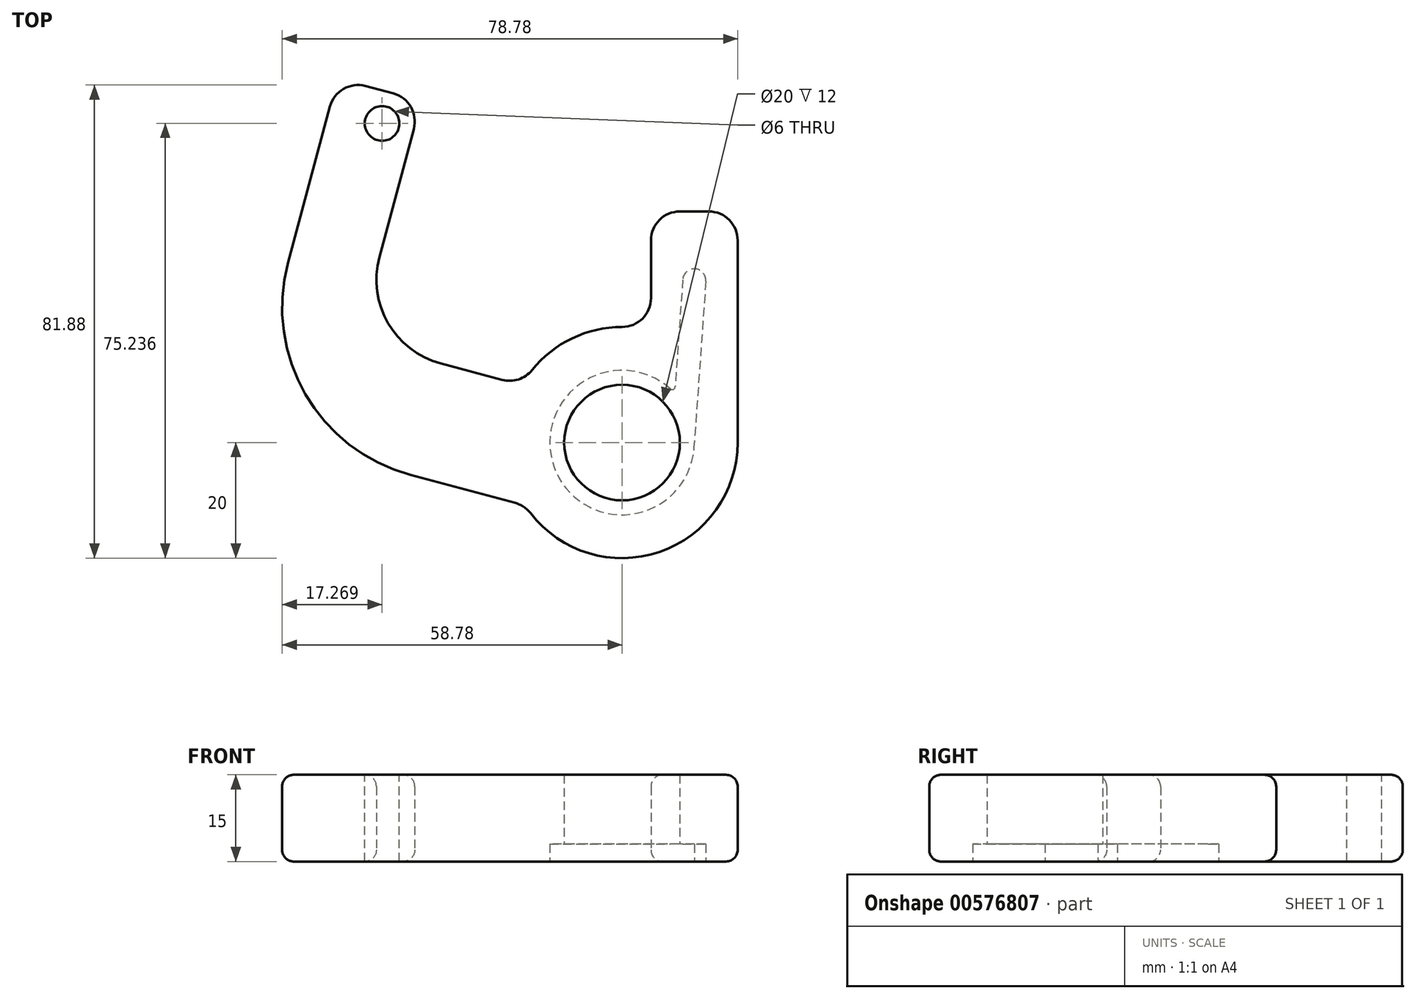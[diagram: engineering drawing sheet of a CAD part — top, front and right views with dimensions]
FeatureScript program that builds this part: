
annotation { "Feature Type Name" : "Feature", "Feature Type Description" : "" }
export const myFeature = defineFeature(function(context is Context, id is Id, definition is map)
    precondition{}
    {
        {
            var Q0;
            Q0=qCreatedBy(makeId("Top.planeOp"),FACE);
            var sketch = newSketch(context, id + "F0", { "sketchPlane" : qUnion([Q0])});
            skCircle(sketch, "E0", {"center": v(0, 0) * mm, "radius": 10 * mm});
            skCircle(sketch, "E1", {"center": v(0, 0) * mm, "radius": 20 * mm});
            skLineSegment(sketch, "E2", {"start": v(20, 0) * mm, "end": v(20, 40) * mm});
            skLineSegment(sketch, "E3", {"start": v(20, 40) * mm, "end": v(5, 40) * mm});
            skLineSegment(sketch, "E4", {"start": v(5, 40) * mm, "end": v(5, 19.36) * mm});
            skLineSegment(sketch, "E5", {"start": v(-17.35, 9.95) * mm, "end": v(-31.37, 13.7) * mm});
            skLineSegment(sketch, "E6", {"start": v(-57.76, 31.13) * mm, "end": v(-49.22, 63) * mm});
            skLineSegment(sketch, "E7", {"start": v(-49.22, 63) * mm, "end": v(-34.73, 59.12) * mm});
            skLineSegment(sketch, "E8", {"start": v(-34.73, 59.12) * mm, "end": v(-41.98, 32.08) * mm});
            skLineSegment(sketch, "E9", {"start": v(0, 0) * mm, "end": v(-115.9, 0) * mm, "construction": true});
            skLineSegment(sketch, "E10", {"start": v(-16.76, -10.92) * mm, "end": v(-36.55, -5.61) * mm});
            skPoint(sketch, "E11.visualSharp", {"position": v(-65.53, 2.15) * mm});
            skArc(sketch, "E11.filletArc", {"start": v(-57.76, 31.13) * mm, "mid": v(-54.77, 8.36) * mm, "end": v(-36.55, -5.61) * mm});
            skPoint(sketch, "E12.visualSharp", {"position": v(-45.86, 17.59) * mm});
            skArc(sketch, "E12.filletArc", {"start": v(-41.98, 32.08) * mm, "mid": v(-40.48, 20.7) * mm, "end": v(-31.37, 13.7) * mm});
            skSolve(sketch);
        }
        {
            var Q0;
            {var subQ0=sQuery(id+"F0.wireOp",EDGE,"E5");Q0=makeQuery(id+"F0.imprint","IMPRINT",FACE,{"disambiguationData":[TD([[makeQuery(id+"F0.imprint","IMPRINT",EDGE,{"derivedFrom":subQ0}),1.0]])]});}
            var Q1;
            Q1=makeQuery(id+"F0.imprint","IMPRINT",FACE,{"disambiguationData":[TD([[makeQuery(id+"F0.imprint","IMPRINT",EDGE,{"derivedFrom":sQuery(id+"F0.wireOp",EDGE,"E0")}),-1.0]])]});
            var Q2;
            {var subQ0=sQuery(id+"F0.wireOp",EDGE,"E2");Q2=makeQuery(id+"F0.imprint","IMPRINT",FACE,{"disambiguationData":[TD([[makeQuery(id+"F0.imprint","IMPRINT",EDGE,{"derivedFrom":subQ0}),1.0]])]});}
            extrude(context, id + "F1", {"entities" : qUnion([Q0, Q1, Q2]), "depth" : 15 * mm, "offsetDistance" : 25 * mm});
        }
        {
            var Q0;
            Q0=makeQuery(id+"F1.opExtrude","SWEPT_EDGE",EDGE,{"disambiguationData":[OSD([sQuery(id+"F0.wireOp",EDGE,"E1"),sQuery(id+"F0.wireOp",EDGE,"E5")])]});
            var Q1;
            Q1=makeQuery(id+"F1.opExtrude","SWEPT_EDGE",EDGE,{"disambiguationData":[OSD([sQuery(id+"F0.wireOp",EDGE,"E1"),sQuery(id+"F0.wireOp",EDGE,"E4")])]});
            fillet(context, id + "F2", {"entities" : qUnion([Q0, Q1]), "radius" : 5 * mm, "tangentPropagation" : true, "allowEdgeOverflow" : false});
        }
        {
            var Q0;
            Q0=makeQuery(id+"F1.opExtrude","SWEPT_EDGE",EDGE,{"disambiguationData":[OSD([sQuery(id+"F0.wireOp",EDGE,"E6"),sQuery(id+"F0.wireOp",EDGE,"E7")])]});
            var Q1;
            Q1=makeQuery(id+"F1.opExtrude","SWEPT_EDGE",EDGE,{"disambiguationData":[OSD([sQuery(id+"F0.wireOp",EDGE,"E7"),sQuery(id+"F0.wireOp",EDGE,"E8")])]});
            var Q2;
            Q2=makeQuery(id+"F1.opExtrude","SWEPT_EDGE",EDGE,{"disambiguationData":[OSD([sQuery(id+"F0.wireOp",EDGE,"E3"),sQuery(id+"F0.wireOp",EDGE,"E4")])]});
            var Q3;
            Q3=makeQuery(id+"F1.opExtrude","SWEPT_EDGE",EDGE,{"disambiguationData":[OSD([sQuery(id+"F0.wireOp",EDGE,"E2"),sQuery(id+"F0.wireOp",EDGE,"E3")])]});
            var Q4;
            Q4=makeQuery(id+"F1.opExtrude","SWEPT_EDGE",EDGE,{"disambiguationData":[OSD([sQuery(id+"F0.wireOp",EDGE,"E1"),sQuery(id+"F0.wireOp",EDGE,"E10")])]});
            fillet(context, id + "F3", {"entities" : qUnion([Q0, Q1, Q2, Q3, Q4]), "radius" : 5 * mm, "tangentPropagation" : true, "allowEdgeOverflow" : false});
        }
        {
            var Q0;
            Q0=makeQuery(id+"F1.opExtrude","CAP_EDGE",EDGE,{"disambiguationData":[OSD([sQuery(id+"F0.wireOp",EDGE,"E6")])],"isStart":false});
            var Q1;
            Q1=makeQuery(id+"F1.opExtrude","CAP_EDGE",EDGE,{"disambiguationData":[OSD([sQuery(id+"F0.wireOp",EDGE,"E5")])],"isStart":true});
            fillet(context, id + "F4", {"entities" : qUnion([Q0, Q1]), "radius" : 2 * mm, "tangentPropagation" : true, "allowEdgeOverflow" : false});
        }
        {
            var Q0;
            Q0=makeQuery(id+"F1.opExtrude","CAP_FACE",FACE,{"disambiguationData":[OSD([sQuery(id+"F0.wireOp",EDGE,"E0"),sQuery(id+"F0.wireOp",EDGE,"E1"),sQuery(id+"F0.wireOp",EDGE,"E2"),sQuery(id+"F0.wireOp",EDGE,"E3"),sQuery(id+"F0.wireOp",EDGE,"E4"),sQuery(id+"F0.wireOp",EDGE,"E5"),sQuery(id+"F0.wireOp",EDGE,"E6"),sQuery(id+"F0.wireOp",EDGE,"E7"),sQuery(id+"F0.wireOp",EDGE,"E8"),sQuery(id+"F0.wireOp",EDGE,"E10"),sQuery(id+"F0.wireOp",EDGE,"E11.filletArc"),sQuery(id+"F0.wireOp",EDGE,"E12.filletArc")])],"isStart":true});
            var sketch = newSketch(context, id + "F5", { "sketchPlane" : qUnion([Q0])});
            skArc(sketch, "E13", {"start": v(12.5, 0) * mm, "mid": v(-11.62, 4.6) * mm, "end": v(9.1, -8.57) * mm});
            skLineSegment(sketch, "E14", {"start": v(14.5, -27.93) * mm, "end": v(12.5, 0) * mm});
            skLineSegment(sketch, "E15", {"start": v(10.5, -28.21) * mm, "end": v(9.1, -8.57) * mm});
            skArc(sketch, "E16", {"start": v(10.5, -28.21) * mm, "mid": v(12.64, -30.07) * mm, "end": v(14.5, -27.93) * mm});
            skSolve(sketch);
        }
        {
            var Q0;
            Q0=makeQuery(id+"F5.imprint","IMPRINT",FACE,{"disambiguationData":[TD([[makeQuery(id+"F5.imprint","IMPRINT",EDGE,{"derivedFrom":sQuery(id+"F5.wireOp",EDGE,"E13")}),1.0]])]});
            extrude(context, id + "F6", {"entities" : qUnion([Q0]), "operationType" : NewBodyOperationType.REMOVE, "oppositeDirection" : true, "depth" : 3 * mm, "offsetDistance" : 25 * mm});
        }
        {
            var Q0;
            Q0=makeQuery(id+"F1.opExtrude","CAP_FACE",FACE,{"disambiguationData":[OSD([sQuery(id+"F0.wireOp",EDGE,"E0"),sQuery(id+"F0.wireOp",EDGE,"E1"),sQuery(id+"F0.wireOp",EDGE,"E2"),sQuery(id+"F0.wireOp",EDGE,"E3"),sQuery(id+"F0.wireOp",EDGE,"E4"),sQuery(id+"F0.wireOp",EDGE,"E5"),sQuery(id+"F0.wireOp",EDGE,"E6"),sQuery(id+"F0.wireOp",EDGE,"E7"),sQuery(id+"F0.wireOp",EDGE,"E8"),sQuery(id+"F0.wireOp",EDGE,"E10"),sQuery(id+"F0.wireOp",EDGE,"E11.filletArc"),sQuery(id+"F0.wireOp",EDGE,"E12.filletArc")])],"isStart":false});
            var sketch = newSketch(context, id + "F7", { "sketchPlane" : qUnion([Q0])});
            skCircle(sketch, "E17", {"center": v(-41.51, 55.24) * mm, "radius": 3 * mm});
            skSolve(sketch);
        }
        {
            var Q0;
            Q0=makeQuery(id+"F7.imprint","IMPRINT",FACE,{"disambiguationData":[TD([[makeQuery(id+"F7.imprint","IMPRINT",EDGE,{"derivedFrom":sQuery(id+"F7.wireOp",EDGE,"E17")}),1.0]])]});
            var Q1;
            Q1=makeQuery(id+"F1.opExtrude","CAP_FACE",FACE,{"disambiguationData":[OSD([sQuery(id+"F0.wireOp",EDGE,"E0"),sQuery(id+"F0.wireOp",EDGE,"E1"),sQuery(id+"F0.wireOp",EDGE,"E2"),sQuery(id+"F0.wireOp",EDGE,"E3"),sQuery(id+"F0.wireOp",EDGE,"E4"),sQuery(id+"F0.wireOp",EDGE,"E5"),sQuery(id+"F0.wireOp",EDGE,"E6"),sQuery(id+"F0.wireOp",EDGE,"E7"),sQuery(id+"F0.wireOp",EDGE,"E8"),sQuery(id+"F0.wireOp",EDGE,"E10"),sQuery(id+"F0.wireOp",EDGE,"E11.filletArc"),sQuery(id+"F0.wireOp",EDGE,"E12.filletArc")])],"isStart":true});
            extrude(context, id + "F8", {"entities" : qUnion([Q0]), "operationType" : NewBodyOperationType.REMOVE, "endBound" : BoundingType.UP_TO_SURFACE, "oppositeDirection" : true, "depth" : 25 * mm, "endBoundEntityFace" : qUnion([Q1]), "offsetDistance" : 25 * mm});
        }
        {
            var Q0;
            Q0=makeQuery(id+"F6.boolean.opBoolean","COPY",EDGE,{"derivedFrom":makeQuery(id+"F6.opExtrude","SWEPT_EDGE",EDGE,{"disambiguationData":[OSD([sQuery(id+"F5.wireOp",EDGE,"E13"),sQuery(id+"F5.wireOp",EDGE,"E15")])]})});
            fillet(context, id + "F9", {"entities" : qUnion([Q0]), "radius" : 0.5 * mm, "tangentPropagation" : true, "allowEdgeOverflow" : false});
        }
    });
